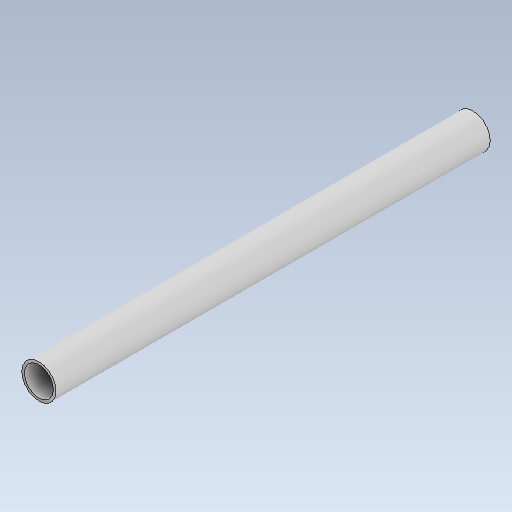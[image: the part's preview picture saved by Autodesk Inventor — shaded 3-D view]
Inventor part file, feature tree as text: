
AUTODESK INVENTOR PART (.ipt)
format: ipt  version: 2020 (Build 240168000, 168)  size: 125,952 bytes
history: native  units: mm
features: extrude x1, sketch x1
ambient origin geometry x8: Origin, YZ Plane, XZ Plane, XY Plane, X Axis, Y Axis, Z Axis, Center Point
bodies: Solid1 (feature_tree)
feature tree (2):
  extrude  "Extrusion1"  Depth=165.196764mm
  sketch  "Sketch1"  dims[d0=11.0mm d1=13.0mm d2=165.196764mm d3=0.0mm]
